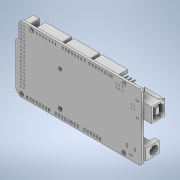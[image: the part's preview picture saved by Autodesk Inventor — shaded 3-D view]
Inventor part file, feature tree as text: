
AUTODESK INVENTOR PART (.ipt)
format: ipt  version: 2021 (Build 250183000, 183)  size: 1,251,328 bytes
history: native  units: in
note: dims shown in document units (in); Inventor stores cm internally (conversion verified against a paired STEP export)
features: fillet x1
ambient origin geometry x8: Origin, YZ Plane, XZ Plane, XY Plane, X Axis, Y Axis, Z Axis, Center Point
bodies: Solid1 (feature_tree)
feature tree (1):
  fillet  "Fillet5"  [1 undecoded]
note: 1 required parameter value undecoded (feature->parameter linkage not recoverable at this tier; creation-order binding heuristic only, values carry confidence <= 0.55)
